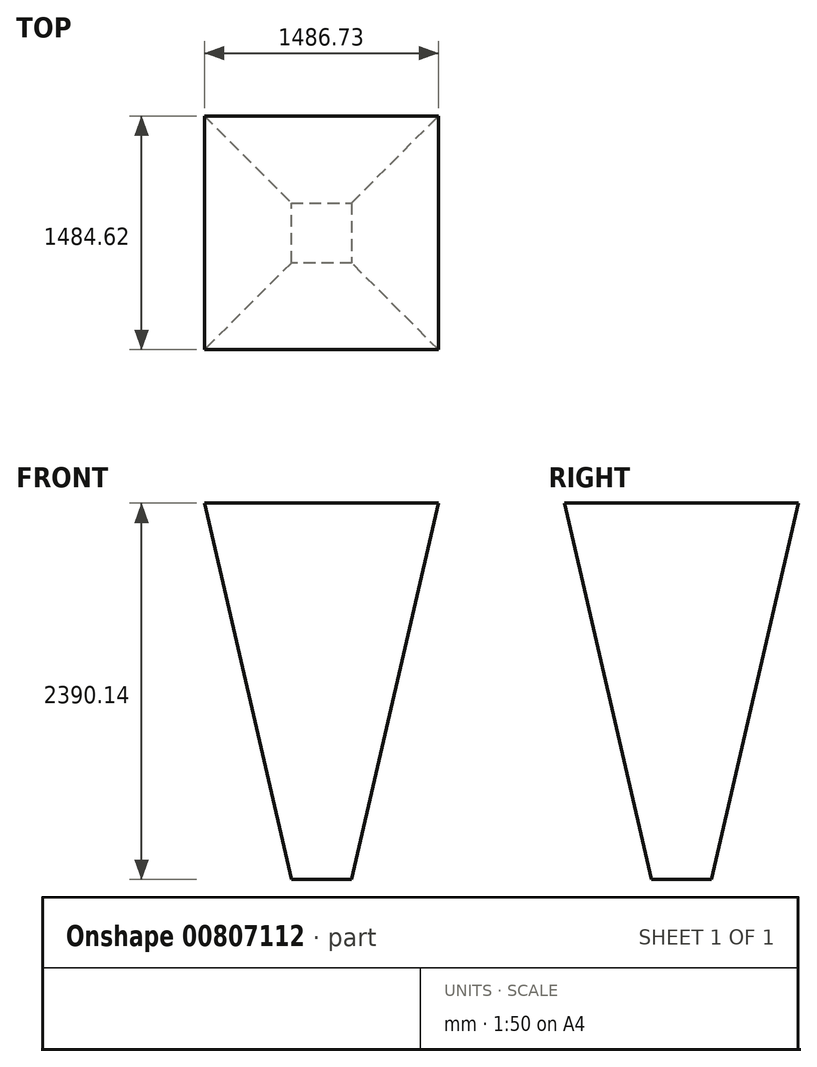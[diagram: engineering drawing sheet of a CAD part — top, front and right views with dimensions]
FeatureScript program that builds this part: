
annotation { "Feature Type Name" : "Feature", "Feature Type Description" : "" }
export const myFeature = defineFeature(function(context is Context, id is Id, definition is map)
    precondition{}
    {
        {
            var Q0;
            Q0=qCreatedBy(makeId("Top.planeOp"),FACE);
            var sketch = newSketch(context, id + "F0", { "sketchPlane" : qUnion([Q0])});
            skLineSegment(sketch, "E0.bottom", {"start": v(191.93, 190) * mm, "end": v(-191.18, 190) * mm});
            skLineSegment(sketch, "E0.top", {"start": v(191.93, -191) * mm, "end": v(-191.18, -191) * mm});
            skLineSegment(sketch, "E0.left", {"start": v(191.93, 190) * mm, "end": v(191.93, -191) * mm});
            skLineSegment(sketch, "E0.right", {"start": v(-191.18, 190) * mm, "end": v(-191.18, -191) * mm});
            skSolve(sketch);
        }
        {
            var Q0;
            Q0=makeQuery(id+"F0.imprint","IMPRINT",FACE,{"disambiguationData":[TD([[makeQuery(id+"F0.imprint","IMPRINT",EDGE,{"derivedFrom":sQuery(id+"F0.wireOp",EDGE,"E0.bottom")}),1.0]])]});
            extrude(context, id + "F1", {"entities" : qUnion([Q0]), "depth" : 75.44 * mm, "offsetDistance" : 25.4 * mm});
        }
        {
            var Q0;
            Q0=makeQuery(id+"F1.opExtrude","SWEPT_EDGE",EDGE,{"disambiguationData":[OSD([sQuery(id+"F0.wireOp",EDGE,"E0.top"),sQuery(id+"F0.wireOp",EDGE,"E0.left")])]});
            var Q1;
            Q1=makeQuery(id+"F1.opExtrude","SWEPT_EDGE",EDGE,{"disambiguationData":[OSD([sQuery(id+"F0.wireOp",EDGE,"E0.top"),sQuery(id+"F0.wireOp",EDGE,"E0.right")])]});
            var Q2;
            Q2=makeQuery(id+"F1.opExtrude","SWEPT_EDGE",EDGE,{"disambiguationData":[OSD([sQuery(id+"F0.wireOp",EDGE,"E0.bottom"),sQuery(id+"F0.wireOp",EDGE,"E0.left")])]});
            var Q3;
            Q3=makeQuery(id+"F1.opExtrude","CAP_EDGE",EDGE,{"disambiguationData":[OSD([sQuery(id+"F0.wireOp",EDGE,"E0.left")])],"isStart":true});
            var Q4;
            Q4=makeQuery(id+"F1.opExtrude","CAP_EDGE",EDGE,{"disambiguationData":[OSD([sQuery(id+"F0.wireOp",EDGE,"E0.left")])],"isStart":false});
            var Q5;
            Q5=makeQuery(id+"F1.opExtrude","CAP_EDGE",EDGE,{"disambiguationData":[OSD([sQuery(id+"F0.wireOp",EDGE,"E0.bottom")])],"isStart":false});
            var Q6;
            Q6=makeQuery(id+"F1.opExtrude","CAP_EDGE",EDGE,{"disambiguationData":[OSD([sQuery(id+"F0.wireOp",EDGE,"E0.right")])],"isStart":false});
            var Q7;
            Q7=makeQuery(id+"F1.opExtrude","CAP_EDGE",EDGE,{"disambiguationData":[OSD([sQuery(id+"F0.wireOp",EDGE,"E0.top")])],"isStart":false});
            var Q8;
            Q8=makeQuery(id+"F1.opExtrude","CAP_EDGE",EDGE,{"disambiguationData":[OSD([sQuery(id+"F0.wireOp",EDGE,"E0.top")])],"isStart":true});
            var Q9;
            Q9=makeQuery(id+"F1.opExtrude","SWEPT_FACE",FACE,{"disambiguationData":[OSD([sQuery(id+"F0.wireOp",EDGE,"E0.right")])]});
            var Q10;
            Q10=makeQuery(id+"F1.opExtrude","CAP_FACE",FACE,{"disambiguationData":[OSD([sQuery(id+"F0.wireOp",EDGE,"E0.bottom"),sQuery(id+"F0.wireOp",EDGE,"E0.top"),sQuery(id+"F0.wireOp",EDGE,"E0.left"),sQuery(id+"F0.wireOp",EDGE,"E0.right")])],"isStart":true});
            fillet(context, id + "F2", {"entities" : qUnion([Q0, Q1, Q2, Q3, Q4, Q5, Q6, Q7, Q8, Q9, Q10]), "radius" : 5.08 * mm, "tangentPropagation" : true, "allowEdgeOverflow" : false});
        }
        {
            var Q0;
            Q0=makeQuery(id+"F0.imprint","IMPRINT",FACE,{"disambiguationData":[TD([[makeQuery(id+"F0.imprint","IMPRINT",EDGE,{"derivedFrom":sQuery(id+"F0.wireOp",EDGE,"E0.bottom")}),1.0]])]});
            var Q1;
            Q1=makeQuery(id+"F1.opExtrude","CAP_FACE",FACE,{"disambiguationData":[OSD([sQuery(id+"F0.wireOp",EDGE,"E0.bottom"),sQuery(id+"F0.wireOp",EDGE,"E0.top"),sQuery(id+"F0.wireOp",EDGE,"E0.left"),sQuery(id+"F0.wireOp",EDGE,"E0.right")])],"isStart":true});
            extrude(context, id + "F3", {"entities" : qUnion([Q0, Q1]), "operationType" : NewBodyOperationType.ADD, "depth" : 2390.14 * mm, "offsetDistance" : 25.4 * mm, "hasDraft" : true, "draftAngle" : 13 * degree});
        }
    });
